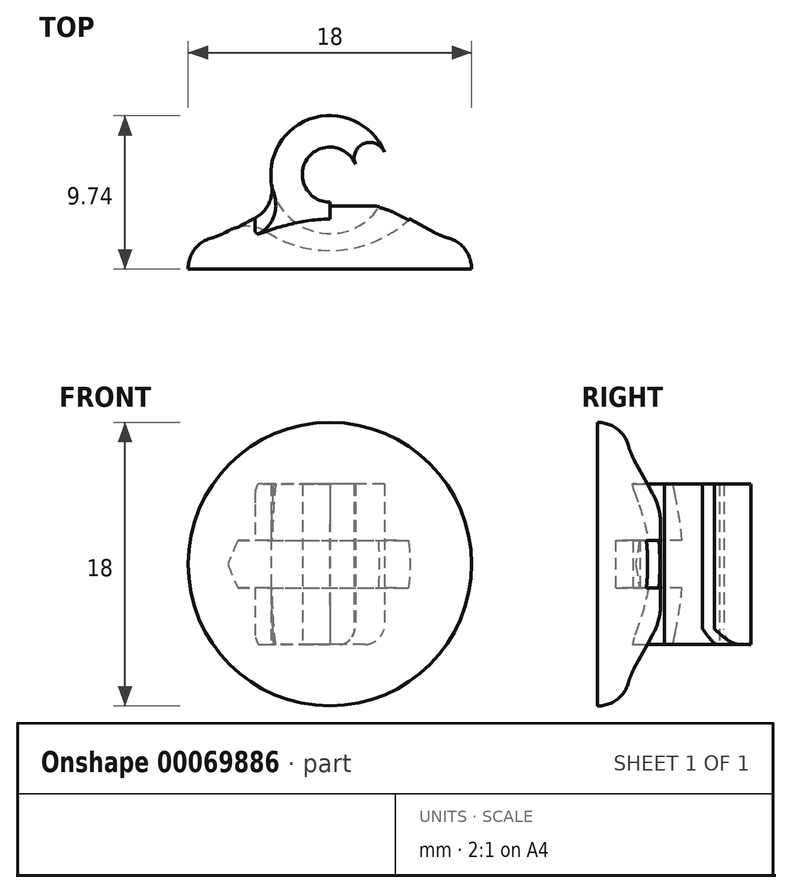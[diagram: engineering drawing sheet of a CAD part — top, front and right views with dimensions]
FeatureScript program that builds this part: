
annotation { "Feature Type Name" : "Feature", "Feature Type Description" : "" }
export const myFeature = defineFeature(function(context is Context, id is Id, definition is map)
    precondition{}
    {
        {
            var Q0;
            Q0=qCreatedBy(makeId("Top.planeOp"),FACE);
            var sketch = newSketch(context, id + "F0", { "sketchPlane" : qUnion([Q0])});
            skLineSegment(sketch, "E0", {"start": v(-9, 0) * mm, "end": v(-9, 0.03) * mm});
            skLineSegment(sketch, "E1", {"start": v(-6.63, 2.32) * mm, "end": v(-4.5, 3.5) * mm});
            skLineSegment(sketch, "E2", {"start": v(-2.56, 4) * mm, "end": v(0, 4) * mm});
            skLineSegment(sketch, "E3", {"start": v(-9, 0) * mm, "end": v(0, 0) * mm});
            skLineSegment(sketch, "E4", {"start": v(0, 0) * mm, "end": v(0, 6) * mm});
            skPoint(sketch, "E5.visualSharp", {"position": v(-9, 2.05) * mm});
            skArc(sketch, "E5.filletArc", {"start": v(-7.52, 1.96) * mm, "mid": v(-8.59, 1.25) * mm, "end": v(-9, 0.03) * mm});
            skPoint(sketch, "E6.visualSharp", {"position": v(-6.76, 2.25) * mm});
            skArc(sketch, "E6.filletArc", {"start": v(-7.52, 1.96) * mm, "mid": v(-7.07, 2.12) * mm, "end": v(-6.63, 2.32) * mm});
            skPoint(sketch, "E7.visualSharp", {"position": v(-3.59, 4) * mm});
            skArc(sketch, "E7.filletArc", {"start": v(-2.56, 4) * mm, "mid": v(-3.56, 3.88) * mm, "end": v(-4.5, 3.5) * mm});
            skCircle(sketch, "E8", {"center": v(0, 6) * mm, "radius": 1.75 * mm});
            skCircle(sketch, "E9", {"center": v(0, 6) * mm, "radius": 3.75 * mm});
            skArc(sketch, "E10", {"start": v(-1.62, 6.66) * mm, "mid": v(-2.17, 7.96) * mm, "end": v(-3.47, 7.41) * mm});
            skArc(sketch, "E11.MirrorCS", {"start": v(1.62, 6.66) * mm, "mid": v(2.17, 7.96) * mm, "end": v(3.47, 7.41) * mm});
            skCircle(sketch, "E12", {"center": v(0, 8.6) * mm, "radius": 7.42 * mm});
            skArc(sketch, "E13", {"start": v(-4, 2.34) * mm, "mid": v(-5.22, 2.72) * mm, "end": v(-6.47, 2.41) * mm});
            skArc(sketch, "E14.MirrorCS", {"start": v(4, 2.34) * mm, "mid": v(5.22, 2.72) * mm, "end": v(6.47, 2.41) * mm});
            skLineSegment(sketch, "E15.MirrorCS", {"start": v(6.63, 2.32) * mm, "end": v(4.5, 3.5) * mm});
            skSolve(sketch);
        }
        {
            var Q0;
            Q0=makeQuery(id+"F0.imprint","IMPRINT",FACE,{"disambiguationData":[TD([[makeQuery(id+"F0.imprint","IMPRINT",EDGE,{"derivedFrom":sQuery(id+"F0.wireOp",EDGE,"E0")}),-1.0]])]});
            var Q1;
            {var subQ0=sQuery(id+"F0.wireOp",EDGE,"dfb681fa-6379-47c4-aa28-4fee6412d9df");Q1=makeQuery(id+"F0.imprint","IMPRINT",FACE,{"disambiguationData":[TD([[makeQuery(id+"F0.imprint","IMPRINT",EDGE,{"derivedFrom":subQ0}),-1.0]])]});}
            var Q2;
            {var subQ0=sQuery(id+"F0.wireOp",EDGE,"E13");Q2=makeQuery(id+"F0.imprint","IMPRINT",FACE,{"disambiguationData":[TD([[makeQuery(id+"F0.imprint","IMPRINT",EDGE,{"derivedFrom":subQ0}),-1.0]])]});}
            var Q3;
            {var subQ0=sQuery(id+"F0.wireOp",EDGE,"E7.filletArc");var subQ1=sQuery(id+"F0.wireOp",EDGE,"E1");var subQ2=makeQuery(id+"F0.imprint","INTERSECT",VERTEX,{"derivedFrom":[subQ1,subQ0]});Q3=makeQuery(id+"F0.imprint","IMPRINT",FACE,{"disambiguationData":[TD([[makeQuery(id+"F0.imprint","IMPRINT",EDGE,{"disambiguationData":[TD([[subQ2,1.0]])],"derivedFrom":subQ1}),-1.0]])]});}
            var Q4;
            {var subQ0=sQuery(id+"F0.wireOp",EDGE,"E2");Q4=makeQuery(id+"F0.imprint","IMPRINT",FACE,{"disambiguationData":[TD([[makeQuery(id+"F0.imprint","IMPRINT",EDGE,{"derivedFrom":subQ0}),-1.0]])]});}
            var Q5;
            Q5=sQuery(id+"F0.wireOp",EDGE,"E4");
            revolve(context, id + "F1", {"entities" : qUnion([Q0, Q1, Q2, Q3, Q4]), "axis" : qUnion([Q5]), "revolveType" : RevolveType.FULL});
        }
        {
            var Q0;
            {var subQ0=sQuery(id+"F0.wireOp",EDGE,"E10");Q0=makeQuery(id+"F0.imprint","IMPRINT",FACE,{"disambiguationData":[TD([[makeQuery(id+"F0.imprint","IMPRINT",EDGE,{"derivedFrom":subQ0}),1.0]])]});}
            var Q1;
            {var subQ0=sQuery(id+"F0.wireOp",EDGE,"E4");var subQ1=sQuery(id+"F0.wireOp",EDGE,"E2");var subQ2=makeQuery(id+"F0.imprint","INTERSECT",VERTEX,{"derivedFrom":[subQ1,subQ0]});Q1=makeQuery(id+"F0.imprint","IMPRINT",FACE,{"disambiguationData":[TD([[makeQuery(id+"F0.imprint","IMPRINT",EDGE,{"disambiguationData":[TD([[subQ2,1.0]])],"derivedFrom":subQ1}),-1.0]])]});}
            var Q2;
            {var subQ0=sQuery(id+"F0.wireOp",EDGE,"E11.MirrorCS");Q2=makeQuery(id+"F0.imprint","IMPRINT",FACE,{"disambiguationData":[TD([[makeQuery(id+"F0.imprint","IMPRINT",EDGE,{"derivedFrom":subQ0}),-1.0]])]});}
            extrude(context, id + "F2", {"entities" : qUnion([Q0, Q1, Q2]), "operationType" : NewBodyOperationType.ADD, "endBound" : BoundingType.SYMMETRIC, "depth" : 10.2 * mm});
        }
        {
            var Q0;
            Q0=makeQuery(id+"F2.boolean.opBoolean","INTERSECT",EDGE,{"disambiguationData":[OD(1.0)],"derivedFrom":[makeQuery(id+"F1.opRevolve","SWEPT_FACE",FACE,{"disambiguationData":[OSD([sQuery(id+"F0.wireOp",EDGE,"E7.filletArc")])]}),makeQuery(id+"F2.opExtrude","SWEPT_FACE",FACE,{"disambiguationData":[OSD([sQuery(id+"F0.wireOp",EDGE,"E9")])]})]});
            var Q1;
            Q1=makeQuery(id+"F2.boolean.opBoolean","INTERSECT",EDGE,{"disambiguationData":[OD(0.0)],"derivedFrom":[makeQuery(id+"F1.opRevolve","SWEPT_FACE",FACE,{"disambiguationData":[OSD([sQuery(id+"F0.wireOp",EDGE,"E7.filletArc")])]}),makeQuery(id+"F2.opExtrude","SWEPT_FACE",FACE,{"disambiguationData":[OSD([sQuery(id+"F0.wireOp",EDGE,"E9")])]})]});
            var Q2;
            Q2=makeQuery(id+"F2.boolean.opBoolean","INTERSECT",EDGE,{"disambiguationData":[OD(1.0)],"derivedFrom":[makeQuery(id+"F1.opRevolve","SWEPT_FACE",FACE,{"disambiguationData":[OSD([sQuery(id+"F0.wireOp",EDGE,"E2")])]}),makeQuery(id+"F2.opExtrude","SWEPT_FACE",FACE,{"disambiguationData":[OSD([sQuery(id+"F0.wireOp",EDGE,"E9")])]})]});
            var Q3;
            Q3=makeQuery(id+"F2.boolean.opBoolean","INTERSECT",EDGE,{"disambiguationData":[OD(3.0)],"derivedFrom":[makeQuery(id+"F1.opRevolve","SWEPT_FACE",FACE,{"disambiguationData":[OSD([sQuery(id+"F0.wireOp",EDGE,"E7.filletArc")])]}),makeQuery(id+"F2.opExtrude","SWEPT_FACE",FACE,{"disambiguationData":[OSD([sQuery(id+"F0.wireOp",EDGE,"E9")])]})]});
            var Q4;
            Q4=makeQuery(id+"F2.boolean.opBoolean","INTERSECT",EDGE,{"disambiguationData":[OD(3.0)],"derivedFrom":[makeQuery(id+"F1.opRevolve","SWEPT_FACE",FACE,{"disambiguationData":[OSD([sQuery(id+"F0.wireOp",EDGE,"E1")])]}),makeQuery(id+"F2.opExtrude","SWEPT_FACE",FACE,{"disambiguationData":[OSD([sQuery(id+"F0.wireOp",EDGE,"E9")])]})]});
            var Q5;
            Q5=makeQuery(id+"F2.boolean.opBoolean","INTERSECT",EDGE,{"disambiguationData":[OD(2.0)],"derivedFrom":[makeQuery(id+"F1.opRevolve","SWEPT_FACE",FACE,{"disambiguationData":[OSD([sQuery(id+"F0.wireOp",EDGE,"E7.filletArc")])]}),makeQuery(id+"F2.opExtrude","SWEPT_FACE",FACE,{"disambiguationData":[OSD([sQuery(id+"F0.wireOp",EDGE,"E9")])]})]});
            var Q6;
            Q6=makeQuery(id+"F2.boolean.opBoolean","INTERSECT",EDGE,{"disambiguationData":[OD(2.0)],"derivedFrom":[makeQuery(id+"F1.opRevolve","SWEPT_FACE",FACE,{"disambiguationData":[OSD([sQuery(id+"F0.wireOp",EDGE,"E1")])]}),makeQuery(id+"F2.opExtrude","SWEPT_FACE",FACE,{"disambiguationData":[OSD([sQuery(id+"F0.wireOp",EDGE,"E9")])]})]});
            fillet(context, id + "F3", {"entities" : qUnion([Q0, Q1, Q2, Q3, Q4, Q5, Q6]), "radius" : 2 * mm, "tangentPropagation" : true, "allowEdgeOverflow" : false});
        }
        {
            var Q0;
            Q0=makeQuery(id+"F2.opExtrude","CAP_EDGE",EDGE,{"disambiguationData":[OSD([sQuery(id+"F0.wireOp",EDGE,"E10")])],"isStart":false});
            var Q1;
            Q1=makeQuery(id+"F2.opExtrude","CAP_EDGE",EDGE,{"disambiguationData":[OSD([sQuery(id+"F0.wireOp",EDGE,"E11.MirrorCS")])],"isStart":true});
            fillet(context, id + "F4", {"entities" : qUnion([Q0, Q1]), "radius" : 1 * mm, "tangentPropagation" : true, "allowEdgeOverflow" : false});
        }
        {
            var Q0;
            {var subQ0=sQuery(id+"F0.wireOp",EDGE,"E13");Q0=makeQuery(id+"F0.imprint","IMPRINT",FACE,{"disambiguationData":[TD([[makeQuery(id+"F0.imprint","IMPRINT",EDGE,{"derivedFrom":subQ0}),-1.0]])]});}
            var Q1;
            {var subQ0=sQuery(id+"F0.wireOp",EDGE,"E7.filletArc");var subQ1=sQuery(id+"F0.wireOp",EDGE,"E1");var subQ2=makeQuery(id+"F0.imprint","INTERSECT",VERTEX,{"derivedFrom":[subQ1,subQ0]});Q1=makeQuery(id+"F0.imprint","IMPRINT",FACE,{"disambiguationData":[TD([[makeQuery(id+"F0.imprint","IMPRINT",EDGE,{"disambiguationData":[TD([[subQ2,1.0]])],"derivedFrom":subQ1}),-1.0]])]});}
            var Q2;
            {var subQ0=sQuery(id+"F0.wireOp",EDGE,"E7.filletArc");var subQ1=sQuery(id+"F0.wireOp",EDGE,"E1");var subQ2=makeQuery(id+"F0.imprint","INTERSECT",VERTEX,{"derivedFrom":[subQ1,subQ0]});Q2=makeQuery(id+"F0.imprint","IMPRINT",FACE,{"disambiguationData":[TD([[makeQuery(id+"F0.imprint","IMPRINT",EDGE,{"disambiguationData":[TD([[subQ2,1.0]])],"derivedFrom":subQ1}),1.0]])]});}
            var Q3;
            {var subQ0=sQuery(id+"F0.wireOp",EDGE,"E14.MirrorCS");Q3=makeQuery(id+"F0.imprint","IMPRINT",FACE,{"disambiguationData":[TD([[makeQuery(id+"F0.imprint","IMPRINT",EDGE,{"derivedFrom":subQ0}),1.0]])]});}
            extrude(context, id + "F5", {"entities" : qUnion([Q0, Q1, Q2, Q3]), "operationType" : NewBodyOperationType.REMOVE, "endBound" : BoundingType.SYMMETRIC, "oppositeDirection" : true, "depth" : 3 * mm});
        }
    });
